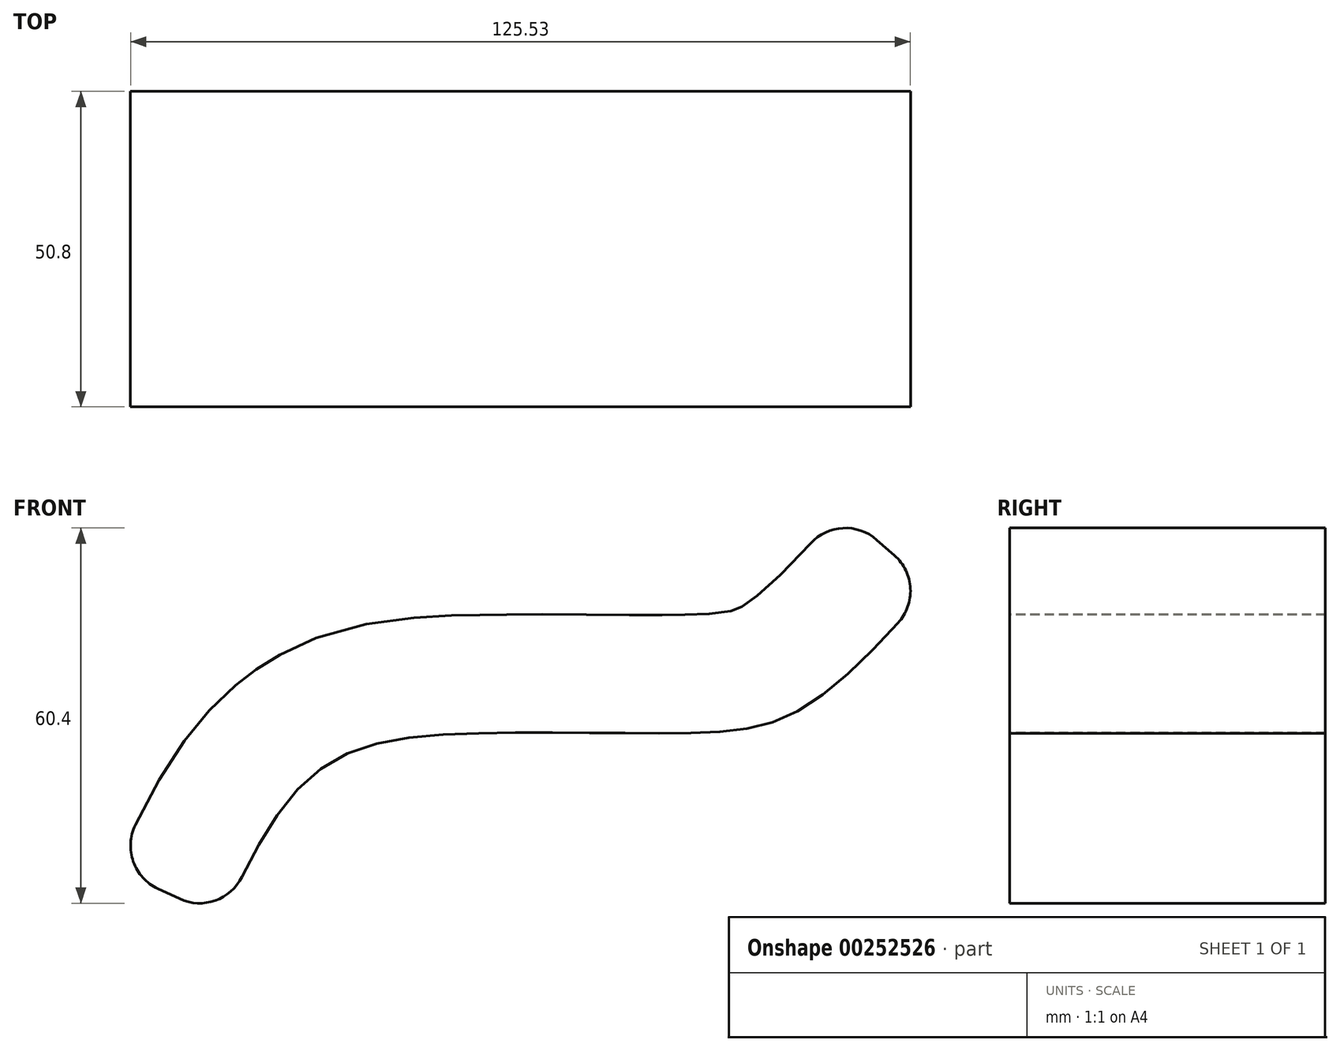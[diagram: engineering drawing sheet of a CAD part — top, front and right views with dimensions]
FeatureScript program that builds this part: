
annotation { "Feature Type Name" : "Feature", "Feature Type Description" : "" }
export const myFeature = defineFeature(function(context is Context, id is Id, definition is map)
    precondition{}
    {
        {
            var Q0;
            Q0=qCreatedBy(makeId("Front.planeOp"),FACE);
            var sketch = newSketch(context, id + "F0", { "sketchPlane" : qUnion([Q0])});
            skFitSpline(sketch, "E0", {"points": [v(-42.04, -29.86) * mm, v(-25.9, -5.53) * mm, v(0, 0) * mm, v(31.7, 0) * mm, v(50.33, 3.4) * mm, v(71.93, 23.52) * mm], "startDerivative": vector(64.82, 139.2) * mm, "endDerivative": vector(103.4, 116.8) * mm});
            skFitSpline(sketch, "E1.0", {"points": [v(-59.3, -21.82) * mm, v(-58.63, -20.37) * mm, v(-57.23, -17.37) * mm, v(-54.92, -12.63) * mm, v(-52.3, -7.73) * mm, v(-49.72, -3.56) * mm, v(-47.33, -0.22) * mm, v(-45.34, 2.27) * mm, v(-43.12, 4.73) * mm, v(-41.05, 6.72) * mm, v(-39.24, 8.26) * mm, v(-38.05, 9.19) * mm, v(-37.06, 9.9) * mm, v(-36.05, 10.62) * mm, v(-34.77, 11.44) * mm, v(-33.2, 12.35) * mm, v(-31.12, 13.46) * mm, v(-27.45, 15.12) * mm, v(-22.27, 16.8) * mm, v(-16.34, 17.98) * mm, v(-11.65, 18.52) * mm, v(-8.04, 18.78) * mm, v(-5.4, 18.91) * mm, v(-3.27, 18.98) * mm, v(-1.6, 19.02) * mm, v(-0.35, 19.05) * mm, v(0.88, 19.07) * mm, v(2.52, 19.09) * mm, v(4.58, 19.1) * mm, v(7.04, 19.12) * mm, v(10.3, 19.12) * mm, v(14.34, 19.1) * mm, v(19.06, 19.07) * mm, v(22.83, 19.05) * mm, v(25.73, 19.04) * mm, v(27.83, 19.03) * mm, v(29.5, 19.04) * mm, v(30.8, 19.04) * mm, v(31.76, 19.05) * mm, v(32.66, 19.06) * mm, v(33.8, 19.08) * mm, v(35.1, 19.12) * mm, v(36.44, 19.18) * mm, v(37.58, 19.27) * mm, v(38.52, 19.38) * mm, v(39.52, 19.55) * mm, v(40.2, 19.73) * mm, v(40.67, 19.9) * mm, v(40.93, 20) * mm, v(41.12, 20.1) * mm, v(41.3, 20.18) * mm, v(41.44, 20.26) * mm, v(41.6, 20.35) * mm, v(41.84, 20.49) * mm, v(42.28, 20.76) * mm, v(42.95, 21.22) * mm, v(43.9, 21.94) * mm, v(44.96, 22.82) * mm, v(46.5, 24.2) * mm, v(48.66, 26.28) * mm, v(51.48, 29.24) * mm, v(54.48, 32.55) * mm, v(56.59, 34.93) * mm, v(57.66, 36.15) * mm]});
            skLineSegment(sketch, "E2", {"start": v(-59.3, -21.82) * mm, "end": v(-42.04, -29.86) * mm});
            skLineSegment(sketch, "E3", {"start": v(57.66, 36.15) * mm, "end": v(71.93, 23.52) * mm});
            skSolve(sketch);
        }
        {
            var Q0;
            Q0 = qSketchRegion(id + "F0", true);
            extrude(context, id + "F1", {"entities" : qUnion([Q0]), "depth" : 50.8 * mm});
        }
        {
            var Q0;
            Q0=makeQuery(id+"F1.opExtrude","SWEPT_EDGE",EDGE,{"disambiguationData":[OSD([sQuery(id+"F0.wireOp",EDGE,"E1.0"),sQuery(id+"F0.wireOp",EDGE,"E3")])]});
            var Q1;
            Q1=makeQuery(id+"F1.opExtrude","SWEPT_EDGE",EDGE,{"disambiguationData":[OSD([sQuery(id+"F0.wireOp",EDGE,"E0"),sQuery(id+"F0.wireOp",EDGE,"E3")])]});
            var Q2;
            Q2=makeQuery(id+"F1.opExtrude","SWEPT_EDGE",EDGE,{"disambiguationData":[OSD([sQuery(id+"F0.wireOp",EDGE,"E1.0"),sQuery(id+"F0.wireOp",EDGE,"E2")])]});
            var Q3;
            Q3=makeQuery(id+"F1.opExtrude","SWEPT_EDGE",EDGE,{"disambiguationData":[OSD([sQuery(id+"F0.wireOp",EDGE,"E0"),sQuery(id+"F0.wireOp",EDGE,"E2")])]});
            fillet(context, id + "F2", {"entities" : qUnion([Q0, Q1, Q2, Q3]), "radius" : 7.62 * mm, "tangentPropagation" : true, "allowEdgeOverflow" : false});
        }
    });
